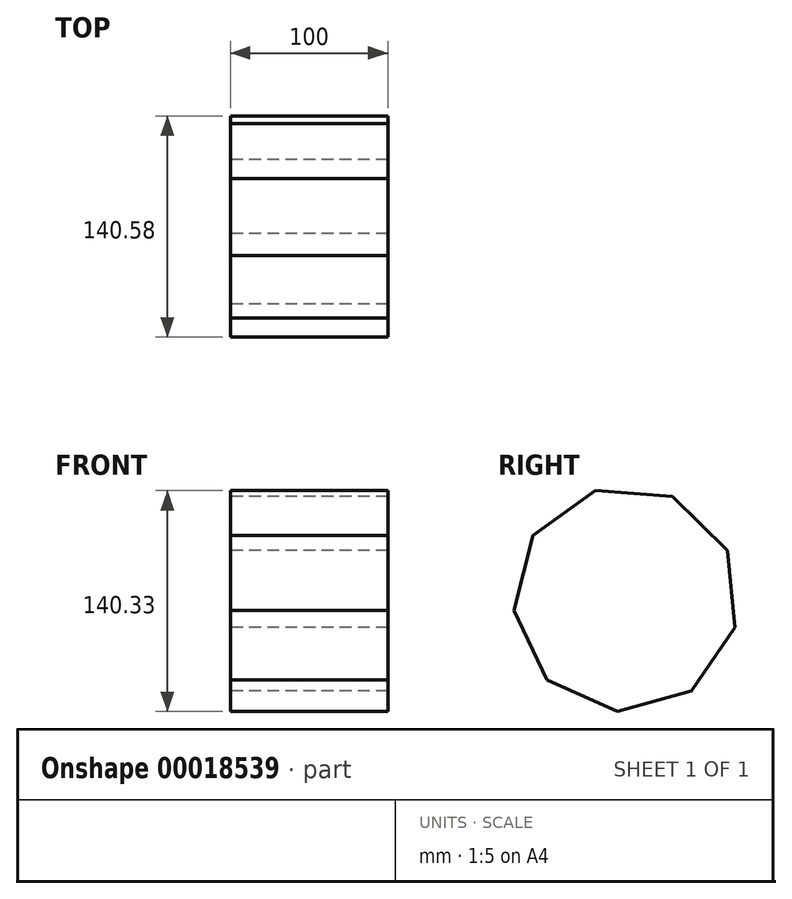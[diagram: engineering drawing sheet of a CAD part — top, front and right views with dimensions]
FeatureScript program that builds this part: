
annotation { "Feature Type Name" : "Feature", "Feature Type Description" : "" }
export const myFeature = defineFeature(function(context is Context, id is Id, definition is map)
    precondition{}
    {
        {
            var Q0;
            Q0=qCreatedBy(makeId("Right.planeOp"),FACE);
            var sketch = newSketch(context, id + "F0", { "sketchPlane" : qUnion([Q0])});
            skCircle(sketch, "E0.cCircle", {"center": v(36.27, 38.35) * mm, "radius": 71.59 * mm, "construction": true});
            skLineSegment(sketch, "E0.0", {"start": v(-13.83, -12.78) * mm, "end": v(-34.98, 31.38) * mm});
            skLineSegment(sketch, "E0.1", {"start": v(-34.98, 31.38) * mm, "end": v(-22.8, 78.8) * mm});
            skLineSegment(sketch, "E0.2", {"start": v(-22.8, 78.8) * mm, "end": v(17.03, 107.3) * mm});
            skLineSegment(sketch, "E0.3", {"start": v(17.03, 107.3) * mm, "end": v(65.85, 103.54) * mm});
            skLineSegment(sketch, "E0.4", {"start": v(65.85, 103.54) * mm, "end": v(100.83, 69.28) * mm});
            skLineSegment(sketch, "E0.5", {"start": v(100.83, 69.28) * mm, "end": v(105.6, 20.54) * mm});
            skLineSegment(sketch, "E0.6", {"start": v(105.6, 20.54) * mm, "end": v(77.93, -19.86) * mm});
            skLineSegment(sketch, "E0.7", {"start": v(77.93, -19.86) * mm, "end": v(30.76, -33.02) * mm});
            skLineSegment(sketch, "E0.8", {"start": v(30.76, -33.02) * mm, "end": v(-13.83, -12.78) * mm});
            skSolve(sketch);
        }
        {
            var Q0;
            Q0=makeQuery(id+"F0.imprint","IMPRINT",FACE,{"disambiguationData":[TD([[makeQuery(id+"F0.imprint","IMPRINT",EDGE,{"derivedFrom":sQuery(id+"F0.wireOp",EDGE,"E0.0")}),-1.0]])]});
            extrude(context, id + "F1", {"entities" : qUnion([Q0]), "depth" : 100 * mm, "offsetDistance" : 25 * mm});
        }
    });
